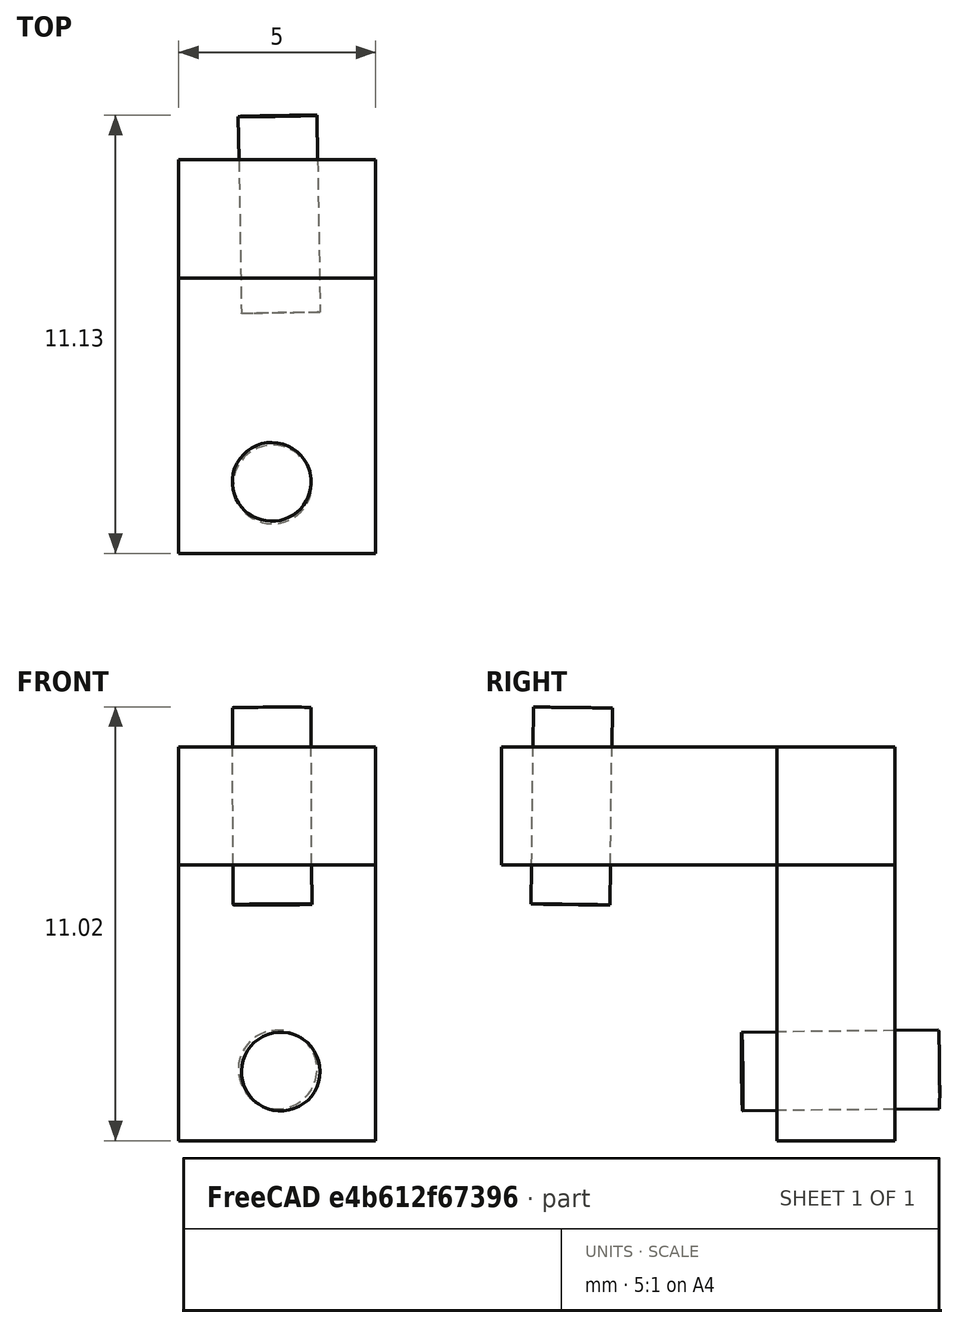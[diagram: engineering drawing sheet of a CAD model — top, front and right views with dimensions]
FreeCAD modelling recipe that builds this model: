
FCSTD DOCUMENT  (FreeCAD 0.16R6700 (Git))
Label: L Bracket 2 (Not Sized Or Connected)
License: All rights reserved
LicenseURL: http://en.wikipedia.org/wiki/All_rights_reserved
objects: Part::Box×2, Part::Cylinder×2
note: 4 computed .brp shape members not serialized (recipe doc carries the construction recipe); baked Part::Feature solids carry a one-line shape summary decoded from their .brp

FEATURE [Part::Box] Box  label="Vertical Cube"
  Height = 10
  Length = 5
  Width = 3
FEATURE [Part::Box] Box001  label="Horizontal Cube"
  Height = 3
  Length = 10
  Placement = pos=(5,-7,7) rot=(0,0,1;1.5708rad)
  Width = 5
FEATURE [Part::Cylinder] Cylinder  label="Vertical Cyclinder"
  Angle = 360
  Height = 5
  Placement = pos=(2.51433,4.11494,1.80883) rot=(0.325907,0.674751,-0.66219;2.4989rad)
  Radius = 1
FEATURE [Part::Cylinder] Cylinder001  label="Horizontal Cyclinder"
  Angle = 360
  Height = 5
  Placement = pos=(2.38593,-5.2465,6.00193) rot=(-0.365562,-0.131275,-0.921483;0.03575rad)
  Radius = 1
